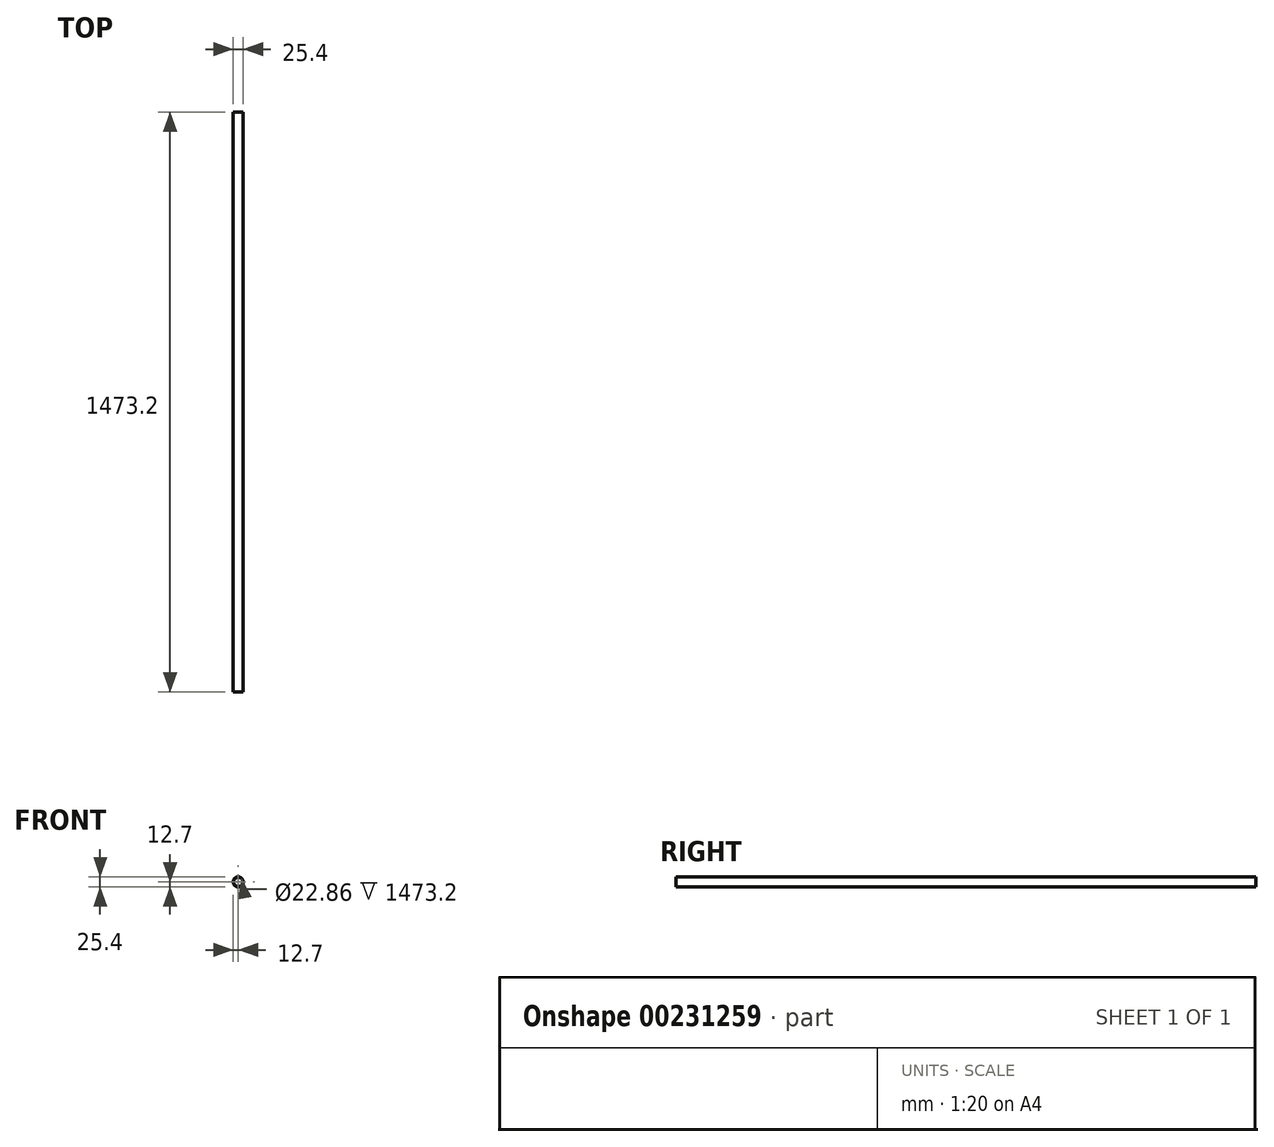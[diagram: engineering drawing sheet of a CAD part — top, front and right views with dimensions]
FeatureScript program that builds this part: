
annotation { "Feature Type Name" : "Feature", "Feature Type Description" : "" }
export const myFeature = defineFeature(function(context is Context, id is Id, definition is map)
    precondition{}
    {
        {
            var Q0;
            Q0=qCreatedBy(makeId("Front.planeOp"),FACE);
            var sketch = newSketch(context, id + "F0", { "sketchPlane" : qUnion([Q0])});
            skCircle(sketch, "E0", {"center": v(0, 0) * mm, "radius": 12.7 * mm});
            skCircle(sketch, "E1.0", {"center": v(0, 0) * mm, "radius": 11.43 * mm});
            skSolve(sketch);
        }
        {
            var Q0;
            Q0 = qSketchRegion(id + "F0", true);
            extrude(context, id + "F1", {"entities" : qUnion([Q0]), "depth" : 1473.2 * mm, "symmetric" : true});
        }
    });
